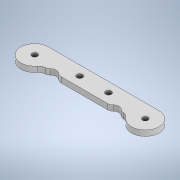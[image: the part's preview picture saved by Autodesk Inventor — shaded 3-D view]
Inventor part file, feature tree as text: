
AUTODESK INVENTOR PART (.ipt)
format: ipt  version: 2020 (Build 240168000, 168)  size: 165,376 bytes
history: native  units: in
note: dims shown in document units (in); Inventor stores cm internally (conversion verified against a paired STEP export)
features: fillet x2, extrude x1, sketch x1
ambient origin geometry x8: Origin, YZ Plane, XZ Plane, XY Plane, X Axis, Y Axis, Z Axis, Center Point
bodies: Solid1 (feature_tree)
feature tree (4):
  extrude  "Extrusion1"  Depth=0.4151in
  fillet  "Fillet2"  Radius=0.122in
  fillet  "Fillet3"  Radius=0.122in
  sketch  "Sketch1"  dims[d0=0.3937in d1=0.3937in d2=0.5906in d3=0.5906in d4=0.122in d5=0.122in d6=0.122in d7=0.1181in d8=0.0in d13=0.4151in d14=0.122in d15=0.122in d16=0.2559in d17=0.2559in d18=0.1181in d19=0.1575in d20=0.2165in]
